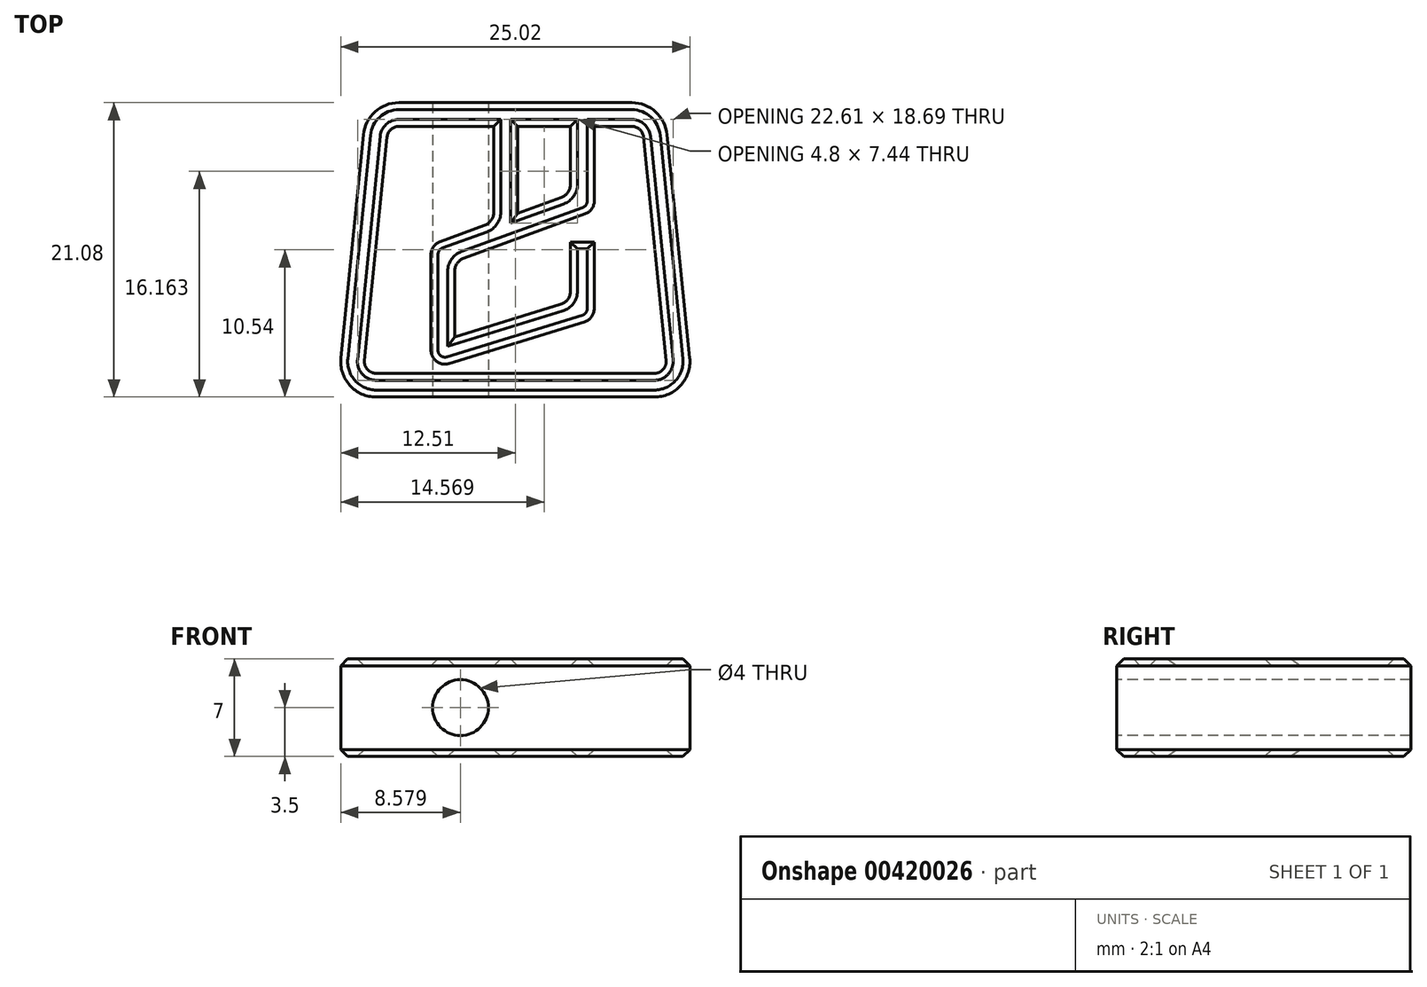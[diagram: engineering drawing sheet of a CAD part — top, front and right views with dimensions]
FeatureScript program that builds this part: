
annotation { "Feature Type Name" : "Feature", "Feature Type Description" : "" }
export const myFeature = defineFeature(function(context is Context, id is Id, definition is map)
    precondition{}
    {
        {
            var Q0;
            Q0=qCreatedBy(makeId("Top.planeOp"),FACE);
            var sketch = newSketch(context, id + "F0", { "sketchPlane" : qUnion([Q0])});
            skLineSegment(sketch, "E0", {"start": v(0.16, 2.62) * mm, "end": v(3.3, 3.76) * mm});
            skLineSegment(sketch, "E1", {"start": v(0.16, 8.84) * mm, "end": v(0.16, 2.62) * mm});
            skLineSegment(sketch, "E2", {"start": v(3.96, 8.84) * mm, "end": v(0.16, 8.84) * mm});
            skLineSegment(sketch, "E3", {"start": v(3.96, 4.7) * mm, "end": v(3.96, 8.84) * mm});
            skArc(sketch, "E4", {"start": v(3.3, 3.76) * mm, "mid": v(3.78, 4.13) * mm, "end": v(3.96, 4.7) * mm});
            skLineSegment(sketch, "E5", {"start": v(-9.2, 8.08) * mm, "end": v(-10.8, -7.9) * mm});
            skArc(sketch, "E6", {"start": v(-8.35, 8.84) * mm, "mid": v(-8.92, 8.62) * mm, "end": v(-9.2, 8.08) * mm});
            skLineSegment(sketch, "E7", {"start": v(-1.54, 8.84) * mm, "end": v(-8.35, 8.84) * mm});
            skLineSegment(sketch, "E8", {"start": v(-1.54, 8.84) * mm, "end": v(-1.54, 2.7) * mm});
            skArc(sketch, "E9", {"start": v(-2.2, 1.76) * mm, "mid": v(-1.72, 2.13) * mm, "end": v(-1.54, 2.7) * mm});
            skLineSegment(sketch, "E10", {"start": v(-5.38, 0.6) * mm, "end": v(-2.2, 1.76) * mm});
            skArc(sketch, "E11", {"start": v(-6.04, -0.34) * mm, "mid": v(-5.86, 0.23) * mm, "end": v(-5.38, 0.6) * mm});
            skLineSegment(sketch, "E12", {"start": v(-6.04, -7.19) * mm, "end": v(-6.04, -0.34) * mm});
            skArc(sketch, "E13", {"start": v(-4.75, -8.14) * mm, "mid": v(-5.64, -8) * mm, "end": v(-6.04, -7.19) * mm});
            skLineSegment(sketch, "E14", {"start": v(4.95, -5.16) * mm, "end": v(-4.75, -8.14) * mm});
            skArc(sketch, "E15", {"start": v(5.66, -4.2) * mm, "mid": v(5.46, -4.8) * mm, "end": v(4.95, -5.16) * mm});
            skLineSegment(sketch, "E16", {"start": v(5.66, 0.57) * mm, "end": v(5.66, -4.2) * mm});
            skLineSegment(sketch, "E17", {"start": v(3.96, 0.57) * mm, "end": v(5.66, 0.57) * mm});
            skLineSegment(sketch, "E18", {"start": v(3.96, 0.57) * mm, "end": v(3.96, -2.94) * mm});
            skArc(sketch, "E19", {"start": v(3.25, -3.9) * mm, "mid": v(3.76, -3.54) * mm, "end": v(3.96, -2.94) * mm});
            skLineSegment(sketch, "E20", {"start": v(3.25, -3.9) * mm, "end": v(-4.34, -6.24) * mm});
            skLineSegment(sketch, "E21", {"start": v(-4.34, -6.24) * mm, "end": v(-4.34, -1.53) * mm});
            skArc(sketch, "E22", {"start": v(-3.68, -0.6) * mm, "mid": v(-4.16, -0.96) * mm, "end": v(-4.34, -1.53) * mm});
            skLineSegment(sketch, "E23", {"start": v(-3.68, -0.6) * mm, "end": v(5, 2.57) * mm});
            skArc(sketch, "E24", {"start": v(5.66, 3.51) * mm, "mid": v(5.48, 2.94) * mm, "end": v(5, 2.57) * mm});
            skLineSegment(sketch, "E25", {"start": v(5.66, 3.51) * mm, "end": v(5.66, 8.84) * mm});
            skLineSegment(sketch, "E26", {"start": v(8.35, 8.84) * mm, "end": v(5.66, 8.84) * mm});
            skArc(sketch, "E27", {"start": v(9.2, 8.08) * mm, "mid": v(8.92, 8.62) * mm, "end": v(8.35, 8.84) * mm});
            skLineSegment(sketch, "E28", {"start": v(10.8, -7.9) * mm, "end": v(9.2, 8.08) * mm});
            skArc(sketch, "E29", {"start": v(9.96, -8.84) * mm, "mid": v(10.6, -8.56) * mm, "end": v(10.8, -7.9) * mm});
            skLineSegment(sketch, "E30", {"start": v(-9.96, -8.84) * mm, "end": v(9.96, -8.84) * mm});
            skArc(sketch, "E31", {"start": v(-10.8, -7.9) * mm, "mid": v(-10.6, -8.56) * mm, "end": v(-9.96, -8.84) * mm});
            skArc(sketch, "E32", {"start": v(12.5, -7.74) * mm, "mid": v(11.86, -9.7) * mm, "end": v(9.96, -10.54) * mm});
            skLineSegment(sketch, "E33", {"start": v(10.88, 8.25) * mm, "end": v(12.5, -7.74) * mm});
            skArc(sketch, "E34", {"start": v(8.35, 10.54) * mm, "mid": v(10.06, 9.89) * mm, "end": v(10.88, 8.25) * mm});
            skLineSegment(sketch, "E35", {"start": v(-8.35, 10.54) * mm, "end": v(8.35, 10.54) * mm});
            skArc(sketch, "E36", {"start": v(-10.88, 8.25) * mm, "mid": v(-10.06, 9.89) * mm, "end": v(-8.35, 10.54) * mm});
            skLineSegment(sketch, "E37", {"start": v(-12.5, -7.74) * mm, "end": v(-10.88, 8.25) * mm});
            skArc(sketch, "E38", {"start": v(-9.96, -10.54) * mm, "mid": v(-11.86, -9.7) * mm, "end": v(-12.5, -7.74) * mm});
            skLineSegment(sketch, "E39", {"start": v(9.96, -10.54) * mm, "end": v(-9.96, -10.54) * mm});
            skPoint(sketch, "E40", {"position": v(-3.93, 10.54) * mm});
            skPoint(sketch, "E41.MirrorP", {"position": v(3.93, 10.54) * mm});
            skLineSegment(sketch, "E42", {"start": v(-3.93, 10.54) * mm, "end": v(-3.93, -10.54) * mm, "construction": true});
            skSolve(sketch);
        }
        {
            var Q0;
            Q0=makeQuery(id+"F0.imprint","IMPRINT",FACE,{"disambiguationData":[TD([[makeQuery(id+"F0.imprint","IMPRINT",EDGE,{"derivedFrom":sQuery(id+"F0.wireOp",EDGE,"E0")}),1.0]])]});
            var Q1;
            Q1=makeQuery(id+"F0.imprint","IMPRINT",FACE,{"disambiguationData":[TD([[makeQuery(id+"F0.imprint","IMPRINT",EDGE,{"derivedFrom":sQuery(id+"F0.wireOp",EDGE,"E0")}),-1.0]])]});
            var Q2;
            Q2=makeQuery(id+"F0.imprint","IMPRINT",FACE,{"disambiguationData":[TD([[makeQuery(id+"F0.imprint","IMPRINT",EDGE,{"derivedFrom":sQuery(id+"F0.wireOp",EDGE,"E5")}),1.0]])]});
            extrude(context, id + "F1", {"entities" : qUnion([Q0, Q1, Q2]), "endBound" : BoundingType.SYMMETRIC, "depth" : 6 * mm});
        }
        {
            var Q0;
            Q0=makeQuery(id+"F0.imprint","IMPRINT",FACE,{"disambiguationData":[TD([[makeQuery(id+"F0.imprint","IMPRINT",EDGE,{"derivedFrom":sQuery(id+"F0.wireOp",EDGE,"E0")}),-1.0]])]});
            extrude(context, id + "F2", {"entities" : qUnion([Q0]), "operationType" : NewBodyOperationType.ADD, "endBound" : BoundingType.SYMMETRIC, "depth" : 7 * mm});
        }
        {
            var Q0;
            Q0=makeQuery(id+"F1.opExtrude","SWEPT_FACE",FACE,{"disambiguationData":[OSD([sQuery(id+"F0.wireOp",EDGE,"E35")])]});
            var sketch = newSketch(context, id + "F3", { "sketchPlane" : qUnion([Q0])});
            skPoint(sketch, "E43.0", {"position": v(3.93, 0) * mm});
            skCircle(sketch, "E44", {"center": v(3.93, 0) * mm, "radius": 2 * mm});
            skSolve(sketch);
        }
        {
            var Q0;
            Q0=qCreatedBy(makeId("Top.planeOp"),FACE);
            var sketch = newSketch(context, id + "F4", { "sketchPlane" : qUnion([Q0])});
            skLineSegment(sketch, "E45.0", {"start": v(-3.93, 10.54) * mm, "end": v(-3.93, -10.54) * mm});
            skSolve(sketch);
        }
        {
            var Q0;
            Q0=makeQuery(id+"F3.imprint","IMPRINT",FACE,{"disambiguationData":[TD([[makeQuery(id+"F3.imprint","IMPRINT",EDGE,{"derivedFrom":sQuery(id+"F3.wireOp",EDGE,"E44")}),1.0]])]});
            var Q1;
            Q1=sQuery(id+"F4.wireOp",EDGE,"E45.0");
            sweep(context, id + "F5", {"operationType" : NewBodyOperationType.REMOVE, "profiles" : qUnion([Q0]), "path" : qUnion([Q1])});
        }
        {
            var Q0;
            Q0=makeQuery(id+"F2.opExtrude","CAP_FACE",FACE,{"disambiguationData":[OSD([sQuery(id+"F0.wireOp",EDGE,"E0"),sQuery(id+"F0.wireOp",EDGE,"E1"),sQuery(id+"F0.wireOp",EDGE,"E2"),sQuery(id+"F0.wireOp",EDGE,"E3"),sQuery(id+"F0.wireOp",EDGE,"E4"),sQuery(id+"F0.wireOp",EDGE,"E5"),sQuery(id+"F0.wireOp",EDGE,"E6"),sQuery(id+"F0.wireOp",EDGE,"E7"),sQuery(id+"F0.wireOp",EDGE,"E8"),sQuery(id+"F0.wireOp",EDGE,"E9"),sQuery(id+"F0.wireOp",EDGE,"E10"),sQuery(id+"F0.wireOp",EDGE,"E11"),sQuery(id+"F0.wireOp",EDGE,"E12"),sQuery(id+"F0.wireOp",EDGE,"E13"),sQuery(id+"F0.wireOp",EDGE,"E14"),sQuery(id+"F0.wireOp",EDGE,"E15"),sQuery(id+"F0.wireOp",EDGE,"E16"),sQuery(id+"F0.wireOp",EDGE,"E17"),sQuery(id+"F0.wireOp",EDGE,"E18"),sQuery(id+"F0.wireOp",EDGE,"E19"),sQuery(id+"F0.wireOp",EDGE,"E20"),sQuery(id+"F0.wireOp",EDGE,"E21"),sQuery(id+"F0.wireOp",EDGE,"E22"),sQuery(id+"F0.wireOp",EDGE,"E23"),sQuery(id+"F0.wireOp",EDGE,"E24"),sQuery(id+"F0.wireOp",EDGE,"E25"),sQuery(id+"F0.wireOp",EDGE,"E26"),sQuery(id+"F0.wireOp",EDGE,"E27"),sQuery(id+"F0.wireOp",EDGE,"E28"),sQuery(id+"F0.wireOp",EDGE,"E29"),sQuery(id+"F0.wireOp",EDGE,"E30"),sQuery(id+"F0.wireOp",EDGE,"E31"),sQuery(id+"F0.wireOp",EDGE,"E32"),sQuery(id+"F0.wireOp",EDGE,"E33"),sQuery(id+"F0.wireOp",EDGE,"E34"),sQuery(id+"F0.wireOp",EDGE,"E35"),sQuery(id+"F0.wireOp",EDGE,"E36"),sQuery(id+"F0.wireOp",EDGE,"E37"),sQuery(id+"F0.wireOp",EDGE,"E38"),sQuery(id+"F0.wireOp",EDGE,"E39")])],"isStart":true});
            var Q1;
            Q1=makeQuery(id+"F2.opExtrude","CAP_FACE",FACE,{"disambiguationData":[OSD([sQuery(id+"F0.wireOp",EDGE,"E0"),sQuery(id+"F0.wireOp",EDGE,"E1"),sQuery(id+"F0.wireOp",EDGE,"E2"),sQuery(id+"F0.wireOp",EDGE,"E3"),sQuery(id+"F0.wireOp",EDGE,"E4"),sQuery(id+"F0.wireOp",EDGE,"E5"),sQuery(id+"F0.wireOp",EDGE,"E6"),sQuery(id+"F0.wireOp",EDGE,"E7"),sQuery(id+"F0.wireOp",EDGE,"E8"),sQuery(id+"F0.wireOp",EDGE,"E9"),sQuery(id+"F0.wireOp",EDGE,"E10"),sQuery(id+"F0.wireOp",EDGE,"E11"),sQuery(id+"F0.wireOp",EDGE,"E12"),sQuery(id+"F0.wireOp",EDGE,"E13"),sQuery(id+"F0.wireOp",EDGE,"E14"),sQuery(id+"F0.wireOp",EDGE,"E15"),sQuery(id+"F0.wireOp",EDGE,"E16"),sQuery(id+"F0.wireOp",EDGE,"E17"),sQuery(id+"F0.wireOp",EDGE,"E18"),sQuery(id+"F0.wireOp",EDGE,"E19"),sQuery(id+"F0.wireOp",EDGE,"E20"),sQuery(id+"F0.wireOp",EDGE,"E21"),sQuery(id+"F0.wireOp",EDGE,"E22"),sQuery(id+"F0.wireOp",EDGE,"E23"),sQuery(id+"F0.wireOp",EDGE,"E24"),sQuery(id+"F0.wireOp",EDGE,"E25"),sQuery(id+"F0.wireOp",EDGE,"E26"),sQuery(id+"F0.wireOp",EDGE,"E27"),sQuery(id+"F0.wireOp",EDGE,"E28"),sQuery(id+"F0.wireOp",EDGE,"E29"),sQuery(id+"F0.wireOp",EDGE,"E30"),sQuery(id+"F0.wireOp",EDGE,"E31"),sQuery(id+"F0.wireOp",EDGE,"E32"),sQuery(id+"F0.wireOp",EDGE,"E33"),sQuery(id+"F0.wireOp",EDGE,"E34"),sQuery(id+"F0.wireOp",EDGE,"E35"),sQuery(id+"F0.wireOp",EDGE,"E36"),sQuery(id+"F0.wireOp",EDGE,"E37"),sQuery(id+"F0.wireOp",EDGE,"E38"),sQuery(id+"F0.wireOp",EDGE,"E39")])],"isStart":false});
            chamfer(context, id + "F6", {"entities" : qUnion([Q0, Q1]), "width" : .5 * mm, "tangentPropagation" : true});
        }
    });
